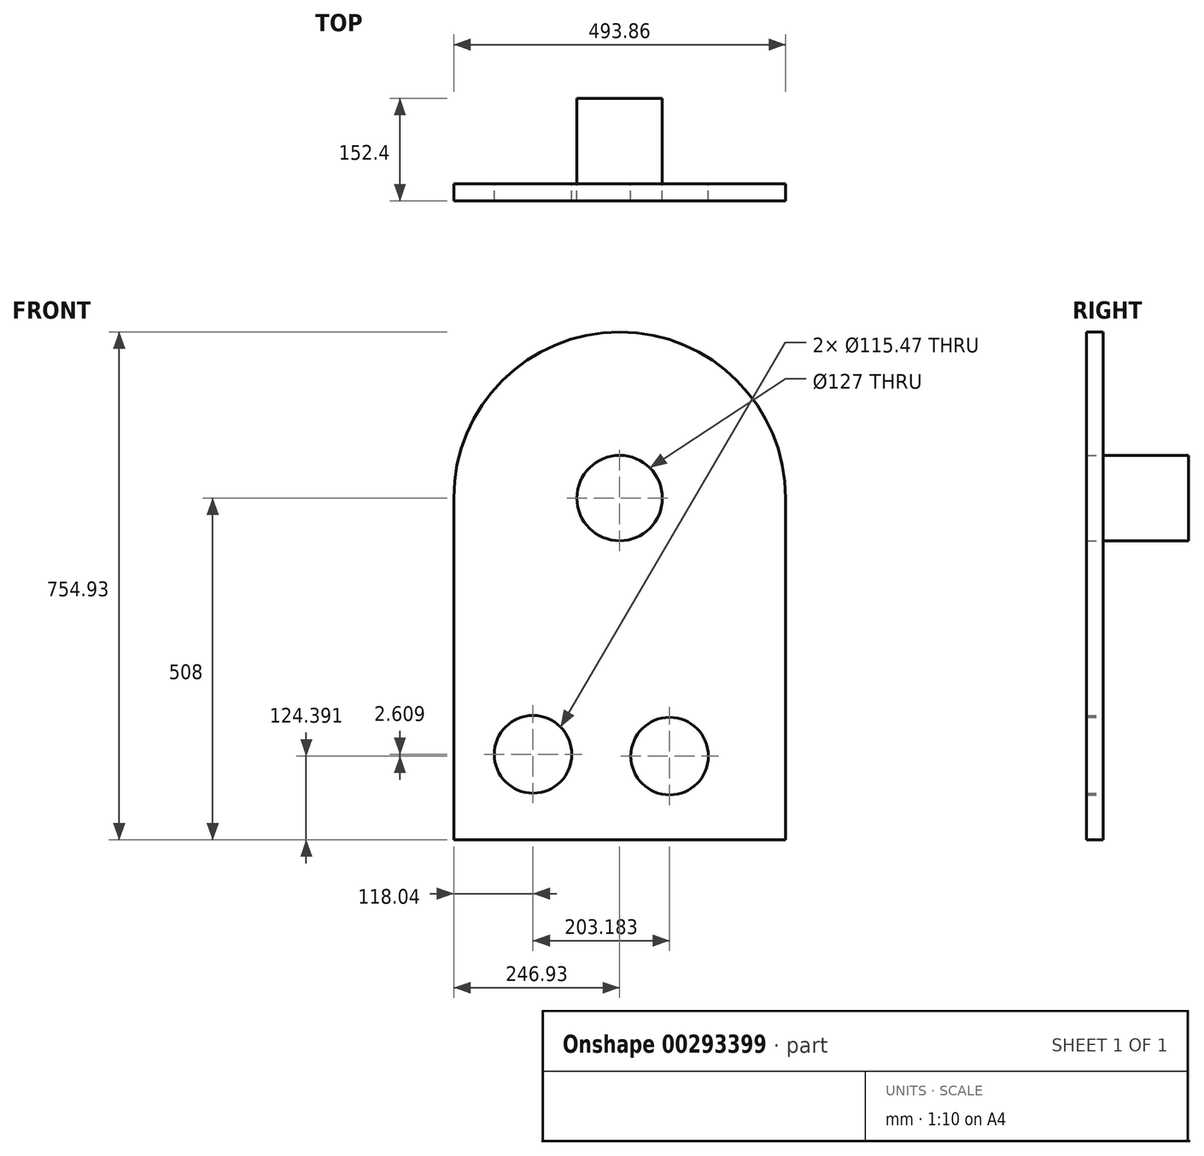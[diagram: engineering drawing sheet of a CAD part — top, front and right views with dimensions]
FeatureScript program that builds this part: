
annotation { "Feature Type Name" : "Feature", "Feature Type Description" : "" }
export const myFeature = defineFeature(function(context is Context, id is Id, definition is map)
    precondition{}
    {
        {
            var Q0;
            Q0=qCreatedBy(makeId("Front.planeOp"),FACE);
            var sketch = newSketch(context, id + "F0", { "sketchPlane" : qUnion([Q0])});
            skLineSegment(sketch, "E0.bottom", {"start": v(-246.93, -254) * mm, "end": v(246.93, -254) * mm});
            skLineSegment(sketch, "E0.top", {"start": v(-246.93, 254) * mm, "end": v(-246.93, 254) * mm});
            skLineSegment(sketch, "E0.left", {"start": v(-246.93, -254) * mm, "end": v(-246.93, 254) * mm});
            skLineSegment(sketch, "E0.right", {"start": v(246.93, -254) * mm, "end": v(246.93, 254) * mm});
            skPoint(sketch, "E0.middle", {"position": v(0, 0) * mm});
            skArc(sketch, "E1", {"start": v(246.93, 254) * mm, "mid": v(0, 500.93) * mm, "end": v(-246.93, 254) * mm});
            skLineSegment(sketch, "E2.trimOffspring", {"start": v(246.93, 254) * mm, "end": v(246.93, 254) * mm});
            skCircle(sketch, "E3", {"center": v(0, 254) * mm, "radius": 63.5 * mm});
            skCircle(sketch, "E4", {"center": v(74.3, -129.6) * mm, "radius": 57.74 * mm});
            skCircle(sketch, "E5", {"center": v(-128.89, -127) * mm, "radius": 57.74 * mm});
            skSolve(sketch);
        }
        {
            var Q0;
            Q0 = qSketchRegion(id + "F0", true);
            extrude(context, id + "F1", {"entities" : qUnion([Q0]), "depth" : 25.4 * mm});
        }
        {
            var Q0;
            Q0=qCreatedBy(makeId("Front.planeOp"),FACE);
            var sketch = newSketch(context, id + "F2", { "sketchPlane" : qUnion([Q0])});
            skCircle(sketch, "E6.0", {"center": v(0, 254) * mm, "radius": 63.5 * mm});
            skSolve(sketch);
        }
        {
            var Q0;
            Q0 = qSketchRegion(id + "F2", true);
            extrude(context, id + "F3", {"entities" : qUnion([Q0]), "operationType" : NewBodyOperationType.ADD, "oppositeDirection" : true, "depth" : 127 * mm});
        }
    });
